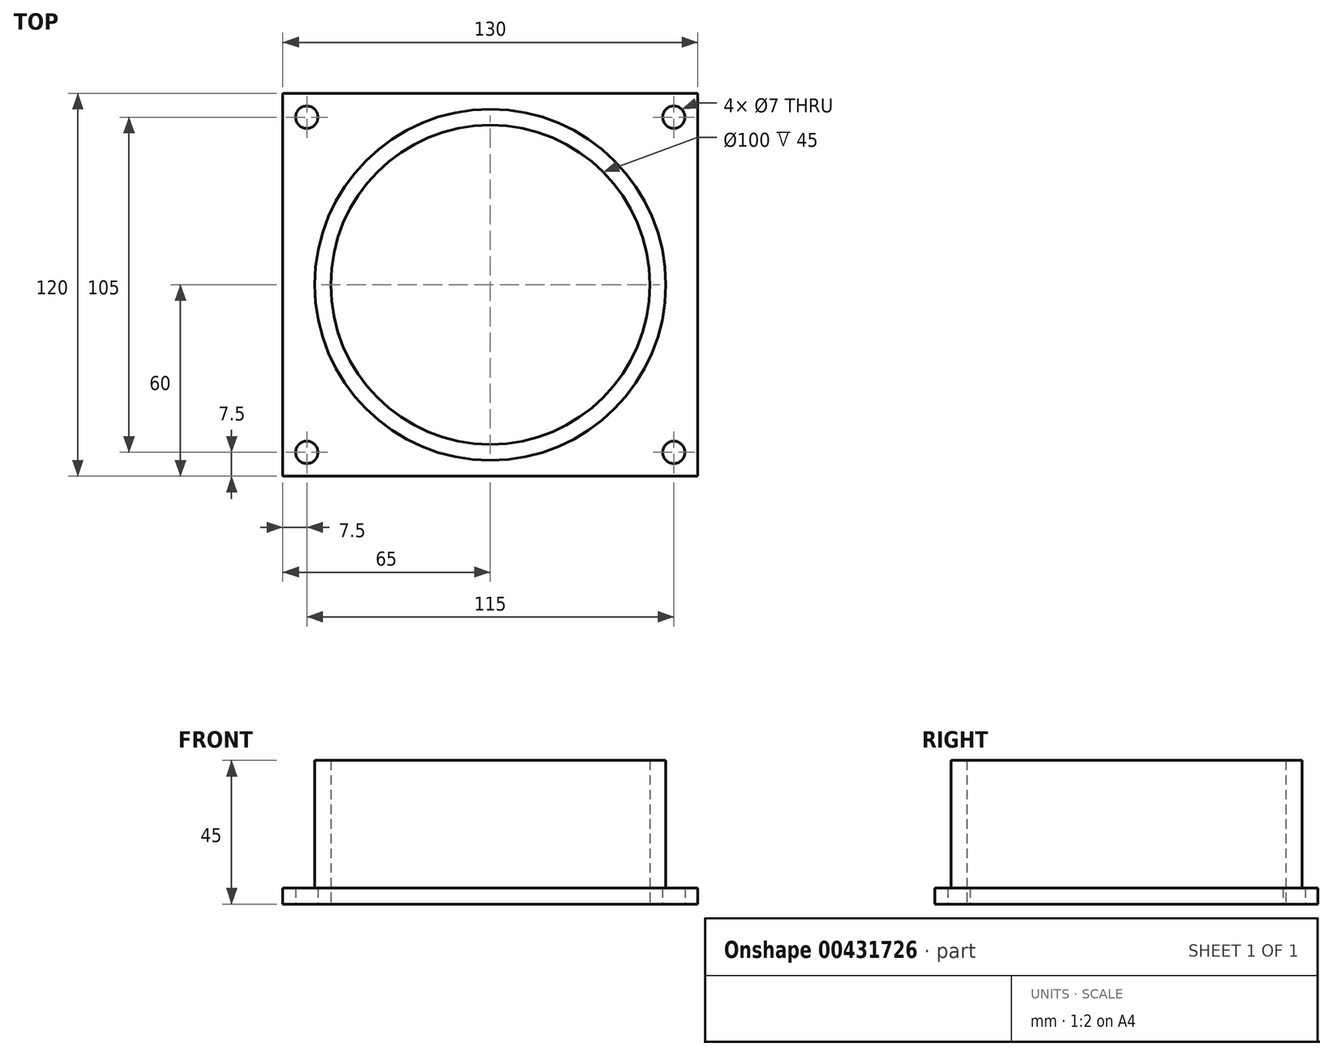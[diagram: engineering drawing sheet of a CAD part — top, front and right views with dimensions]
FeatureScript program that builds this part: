
annotation { "Feature Type Name" : "Feature", "Feature Type Description" : "" }
export const myFeature = defineFeature(function(context is Context, id is Id, definition is map)
    precondition{}
    {
        {
            var Q0;
            Q0=qCreatedBy(makeId("Top.planeOp"),FACE);
            var sketch = newSketch(context, id + "F0", { "sketchPlane" : qUnion([Q0])});
            skLineSegment(sketch, "E0.bottom", {"start": v(0, 0) * mm, "end": v(130, 0) * mm});
            skLineSegment(sketch, "E0.top", {"start": v(0, 120) * mm, "end": v(130, 120) * mm});
            skLineSegment(sketch, "E0.left", {"start": v(0, 0) * mm, "end": v(0, 120) * mm});
            skLineSegment(sketch, "E0.right", {"start": v(130, 0) * mm, "end": v(130, 120) * mm});
            skCircle(sketch, "E1", {"center": v(7.5, 112.5) * mm, "radius": 3.5 * mm});
            skLineSegment(sketch, "E2", {"start": v(65, 131.71) * mm, "end": v(65, -19.28) * mm, "construction": true});
            skPoint(sketch, "E3", {"position": v(65, 120) * mm});
            skLineSegment(sketch, "E4", {"start": v(-11.1, 60) * mm, "end": v(136.86, 60) * mm, "construction": true});
            skPoint(sketch, "E5", {"position": v(0, 60) * mm});
            skCircle(sketch, "E6", {"center": v(122.5, 112.5) * mm, "radius": 3.5 * mm});
            skCircle(sketch, "E7", {"center": v(7.5, 7.5) * mm, "radius": 3.5 * mm});
            skCircle(sketch, "E8", {"center": v(122.5, 7.5) * mm, "radius": 3.5 * mm});
            skPoint(sketch, "E9.middle", {"position": v(65, 60) * mm});
            skCircle(sketch, "E10", {"center": v(65, 60) * mm, "radius": 50 * mm});
            skSolve(sketch);
        }
        {
            var Q0;
            Q0=makeQuery(id+"F0.imprint","IMPRINT",FACE,{"disambiguationData":[TD([[makeQuery(id+"F0.imprint","IMPRINT",EDGE,{"derivedFrom":sQuery(id+"F0.wireOp",EDGE,"E0.bottom")}),1.0]])]});
            extrude(context, id + "F1", {"entities" : qUnion([Q0]), "depth" : 5 * mm});
        }
        {
            var Q0;
            Q0=makeQuery(id+"F1.opExtrude","CAP_FACE",FACE,{"disambiguationData":[OSD([sQuery(id+"F0.wireOp",EDGE,"E0.bottom"),sQuery(id+"F0.wireOp",EDGE,"E0.top"),sQuery(id+"F0.wireOp",EDGE,"E0.left"),sQuery(id+"F0.wireOp",EDGE,"E0.right"),sQuery(id+"F0.wireOp",EDGE,"E1"),sQuery(id+"F0.wireOp",EDGE,"E6"),sQuery(id+"F0.wireOp",EDGE,"E7"),sQuery(id+"F0.wireOp",EDGE,"E8"),sQuery(id+"F0.wireOp",EDGE,"E10")])],"isStart":false});
            var sketch = newSketch(context, id + "F2", { "sketchPlane" : qUnion([Q0])});
            skCircle(sketch, "E11", {"center": v(65, 60) * mm, "radius": 55 * mm});
            skSolve(sketch);
        }
        {
            var Q0;
            Q0=makeQuery(id+"F2.imprint","IMPRINT",FACE,{"disambiguationData":[TD([[makeQuery(id+"F2.imprint","IMPRINT",EDGE,{"derivedFrom":sQuery(id+"F2.wireOp",EDGE,"E11")}),1.0]])]});
            extrude(context, id + "F3", {"entities" : qUnion([Q0]), "operationType" : NewBodyOperationType.ADD, "depth" : 40 * mm});
        }
    });
